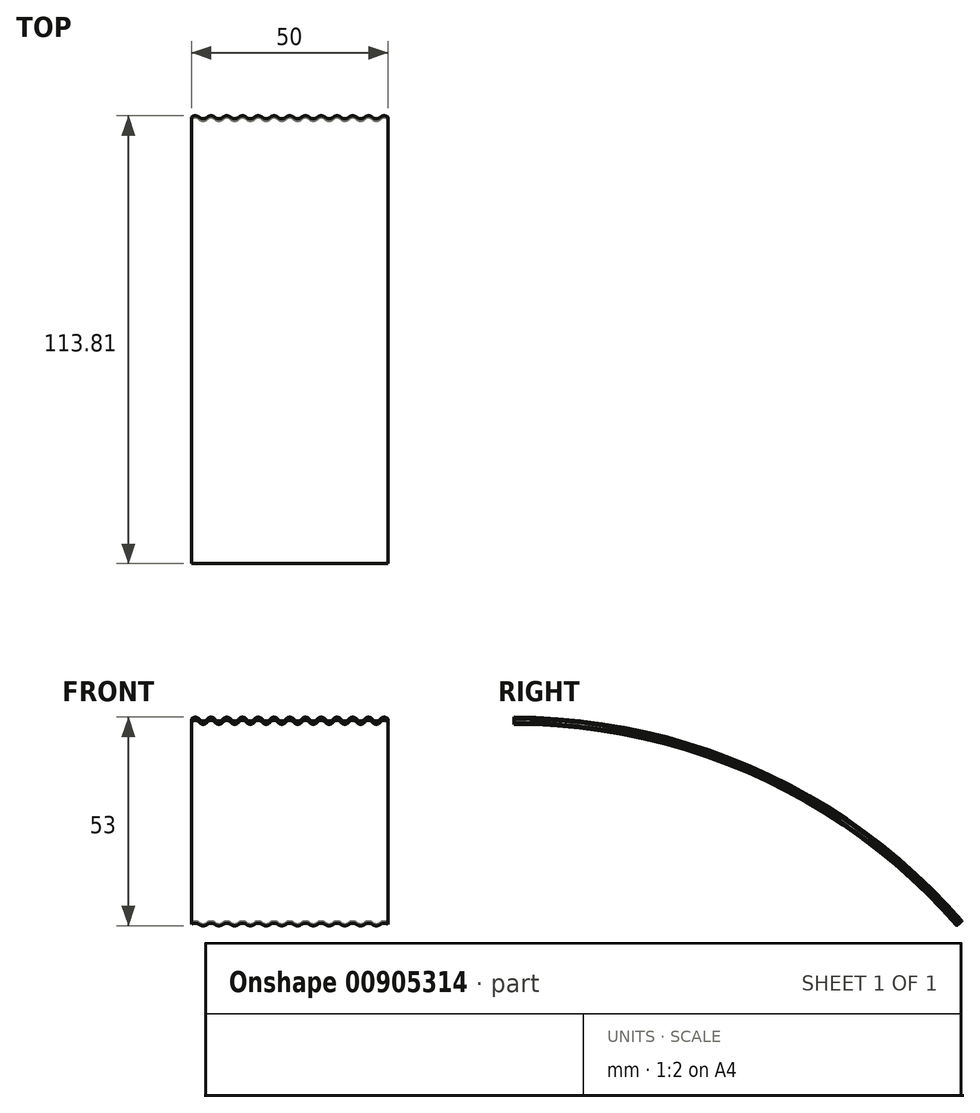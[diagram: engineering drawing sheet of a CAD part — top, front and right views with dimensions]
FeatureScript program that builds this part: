
annotation { "Feature Type Name" : "Feature", "Feature Type Description" : "" }
export const myFeature = defineFeature(function(context is Context, id is Id, definition is map)
    precondition{}
    {
        {
            var Q0;
            Q0=qCreatedBy(makeId("Front.planeOp"),FACE);
            var sketch = newSketch(context, id + "F0", { "sketchPlane" : qUnion([Q0])});
            skArc(sketch, "E0", {"start": v(-19, -0.4) * mm, "mid": v(-20, 0.1) * mm, "end": v(-21, -0.4) * mm});
            skArc(sketch, "E1", {"start": v(-23, -0.4) * mm, "mid": v(-22, -0.9) * mm, "end": v(-21, -0.4) * mm});
            skArc(sketch, "E2", {"start": v(-23, -0.4) * mm, "mid": v(-24, 0.1) * mm, "end": v(-25, -0.4) * mm});
            skArc(sketch, "E3", {"start": v(5, -0.4) * mm, "mid": v(6, -0.9) * mm, "end": v(7, -0.4) * mm});
            skArc(sketch, "E4", {"start": v(9, -0.4) * mm, "mid": v(8, 0.1) * mm, "end": v(7, -0.4) * mm});
            skArc(sketch, "E5", {"start": v(9, -0.4) * mm, "mid": v(10, -0.9) * mm, "end": v(11, -0.4) * mm});
            skArc(sketch, "E6", {"start": v(13, -0.4) * mm, "mid": v(12, 0.1) * mm, "end": v(11, -0.4) * mm});
            skArc(sketch, "E7", {"start": v(13, -0.4) * mm, "mid": v(14, -0.9) * mm, "end": v(15, -0.4) * mm});
            skArc(sketch, "E8", {"start": v(17, -0.4) * mm, "mid": v(16, 0.1) * mm, "end": v(15, -0.4) * mm});
            skArc(sketch, "E9", {"start": v(25, -0.4) * mm, "mid": v(24, 0.1) * mm, "end": v(23, -0.4) * mm});
            skArc(sketch, "E10", {"start": v(21, -0.4) * mm, "mid": v(22, -0.9) * mm, "end": v(23, -0.4) * mm});
            skArc(sketch, "E11", {"start": v(21, -0.4) * mm, "mid": v(20, 0.1) * mm, "end": v(19, -0.4) * mm});
            skArc(sketch, "E12", {"start": v(17, -0.4) * mm, "mid": v(18, -0.9) * mm, "end": v(19, -0.4) * mm});
            skArc(sketch, "E13", {"start": v(5, -0.4) * mm, "mid": v(4, 0.1) * mm, "end": v(3, -0.4) * mm});
            skArc(sketch, "E14", {"start": v(1, -0.4) * mm, "mid": v(2, -0.9) * mm, "end": v(3, -0.4) * mm});
            skArc(sketch, "E15", {"start": v(1, -0.4) * mm, "mid": v(0, 0.1) * mm, "end": v(-1, -0.4) * mm});
            skArc(sketch, "E16", {"start": v(-3, -0.4) * mm, "mid": v(-2, -0.9) * mm, "end": v(-1, -0.4) * mm});
            skArc(sketch, "E17", {"start": v(-3, -0.4) * mm, "mid": v(-4, 0.1) * mm, "end": v(-5, -0.4) * mm});
            skArc(sketch, "E18", {"start": v(-7, -0.4) * mm, "mid": v(-6, -0.9) * mm, "end": v(-5, -0.4) * mm});
            skArc(sketch, "E19", {"start": v(-7, -0.4) * mm, "mid": v(-8, 0.1) * mm, "end": v(-9, -0.4) * mm});
            skArc(sketch, "E20", {"start": v(-11, -0.4) * mm, "mid": v(-10, -0.9) * mm, "end": v(-9, -0.4) * mm});
            skArc(sketch, "E21", {"start": v(-11, -0.4) * mm, "mid": v(-12, 0.1) * mm, "end": v(-13, -0.4) * mm});
            skArc(sketch, "E22", {"start": v(-15, -0.4) * mm, "mid": v(-14, -0.9) * mm, "end": v(-13, -0.4) * mm});
            skArc(sketch, "E23", {"start": v(-15, -0.4) * mm, "mid": v(-16, 0.1) * mm, "end": v(-17, -0.4) * mm});
            skArc(sketch, "E24", {"start": v(-19, -0.4) * mm, "mid": v(-18, -0.9) * mm, "end": v(-17, -0.4) * mm});
            skArc(sketch, "E25", {"start": v(-19, 0.4) * mm, "mid": v(-20, 0.9) * mm, "end": v(-21, 0.4) * mm});
            skArc(sketch, "E26", {"start": v(-23, 0.4) * mm, "mid": v(-22, -0.1) * mm, "end": v(-21, 0.4) * mm});
            skArc(sketch, "E27", {"start": v(-23, 0.4) * mm, "mid": v(-24, 0.9) * mm, "end": v(-25, 0.4) * mm});
            skArc(sketch, "E28", {"start": v(5, 0.4) * mm, "mid": v(6, -0.1) * mm, "end": v(7, 0.4) * mm});
            skArc(sketch, "E29", {"start": v(9, 0.4) * mm, "mid": v(8, 0.9) * mm, "end": v(7, 0.4) * mm});
            skArc(sketch, "E30", {"start": v(9, 0.4) * mm, "mid": v(10, -0.1) * mm, "end": v(11, 0.4) * mm});
            skArc(sketch, "E31", {"start": v(13, 0.4) * mm, "mid": v(12, 0.9) * mm, "end": v(11, 0.4) * mm});
            skArc(sketch, "E32", {"start": v(13, 0.4) * mm, "mid": v(14, -0.1) * mm, "end": v(15, 0.4) * mm});
            skArc(sketch, "E33", {"start": v(17, 0.4) * mm, "mid": v(16, 0.9) * mm, "end": v(15, 0.4) * mm});
            skArc(sketch, "E34", {"start": v(25, 0.4) * mm, "mid": v(24, 0.9) * mm, "end": v(23, 0.4) * mm});
            skArc(sketch, "E35", {"start": v(21, 0.4) * mm, "mid": v(22, -0.1) * mm, "end": v(23, 0.4) * mm});
            skArc(sketch, "E36", {"start": v(21, 0.4) * mm, "mid": v(20, 0.9) * mm, "end": v(19, 0.4) * mm});
            skArc(sketch, "E37", {"start": v(17, 0.4) * mm, "mid": v(18, -0.1) * mm, "end": v(19, 0.4) * mm});
            skArc(sketch, "E38", {"start": v(5, 0.4) * mm, "mid": v(4, 0.9) * mm, "end": v(3, 0.4) * mm});
            skArc(sketch, "E39", {"start": v(1, 0.4) * mm, "mid": v(2, -0.1) * mm, "end": v(3, 0.4) * mm});
            skArc(sketch, "E40", {"start": v(1, 0.4) * mm, "mid": v(0, 0.9) * mm, "end": v(-1, 0.4) * mm});
            skArc(sketch, "E41", {"start": v(-3, 0.4) * mm, "mid": v(-2, -0.1) * mm, "end": v(-1, 0.4) * mm});
            skArc(sketch, "E42", {"start": v(-3, 0.4) * mm, "mid": v(-4, 0.9) * mm, "end": v(-5, 0.4) * mm});
            skArc(sketch, "E43", {"start": v(-7, 0.4) * mm, "mid": v(-6, -0.1) * mm, "end": v(-5, 0.4) * mm});
            skArc(sketch, "E44", {"start": v(-7, 0.4) * mm, "mid": v(-8, 0.9) * mm, "end": v(-9, 0.4) * mm});
            skArc(sketch, "E45", {"start": v(-11, 0.4) * mm, "mid": v(-10, -0.1) * mm, "end": v(-9, 0.4) * mm});
            skArc(sketch, "E46", {"start": v(-11, 0.4) * mm, "mid": v(-12, 0.9) * mm, "end": v(-13, 0.4) * mm});
            skArc(sketch, "E47", {"start": v(-15, 0.4) * mm, "mid": v(-14, -0.1) * mm, "end": v(-13, 0.4) * mm});
            skArc(sketch, "E48", {"start": v(-15, 0.4) * mm, "mid": v(-16, 0.9) * mm, "end": v(-17, 0.4) * mm});
            skArc(sketch, "E49", {"start": v(-19, 0.4) * mm, "mid": v(-18, -0.1) * mm, "end": v(-17, 0.4) * mm});
            skLineSegment(sketch, "E50", {"start": v(-25, 0.4) * mm, "end": v(-25, -0.4) * mm});
            skLineSegment(sketch, "E51", {"start": v(25, 0.4) * mm, "end": v(25, -0.4) * mm});
            skSolve(sketch);
        }
        {
            var Q0;
            Q0=qCreatedBy(makeId("Right.planeOp"),FACE);
            var sketch = newSketch(context, id + "F1", { "sketchPlane" : qUnion([Q0])});
            skLineSegment(sketch, "E52", {"start": v(0, 0) * mm, "end": v(0, -150) * mm, "construction": true});
            skArc(sketch, "E53", {"start": v(0, 0) * mm, "mid": v(62.15, -13.48) * mm, "end": v(113.13, -51.5) * mm});
            skSolve(sketch);
        }
        {
            var Q0;
            Q0=makeQuery(id+"F0.imprint","IMPRINT",FACE,{"disambiguationData":[TD([[makeQuery(id+"F0.imprint","IMPRINT",EDGE,{"derivedFrom":sQuery(id+"F0.wireOp",EDGE,"E0")}),-1.0]])]});
            var Q1;
            Q1=sQuery(id+"F1.wireOp",EDGE,"E53");
            sweep(context, id + "F2", {"profiles" : qUnion([Q0]), "path" : qUnion([Q1])});
        }
    });
